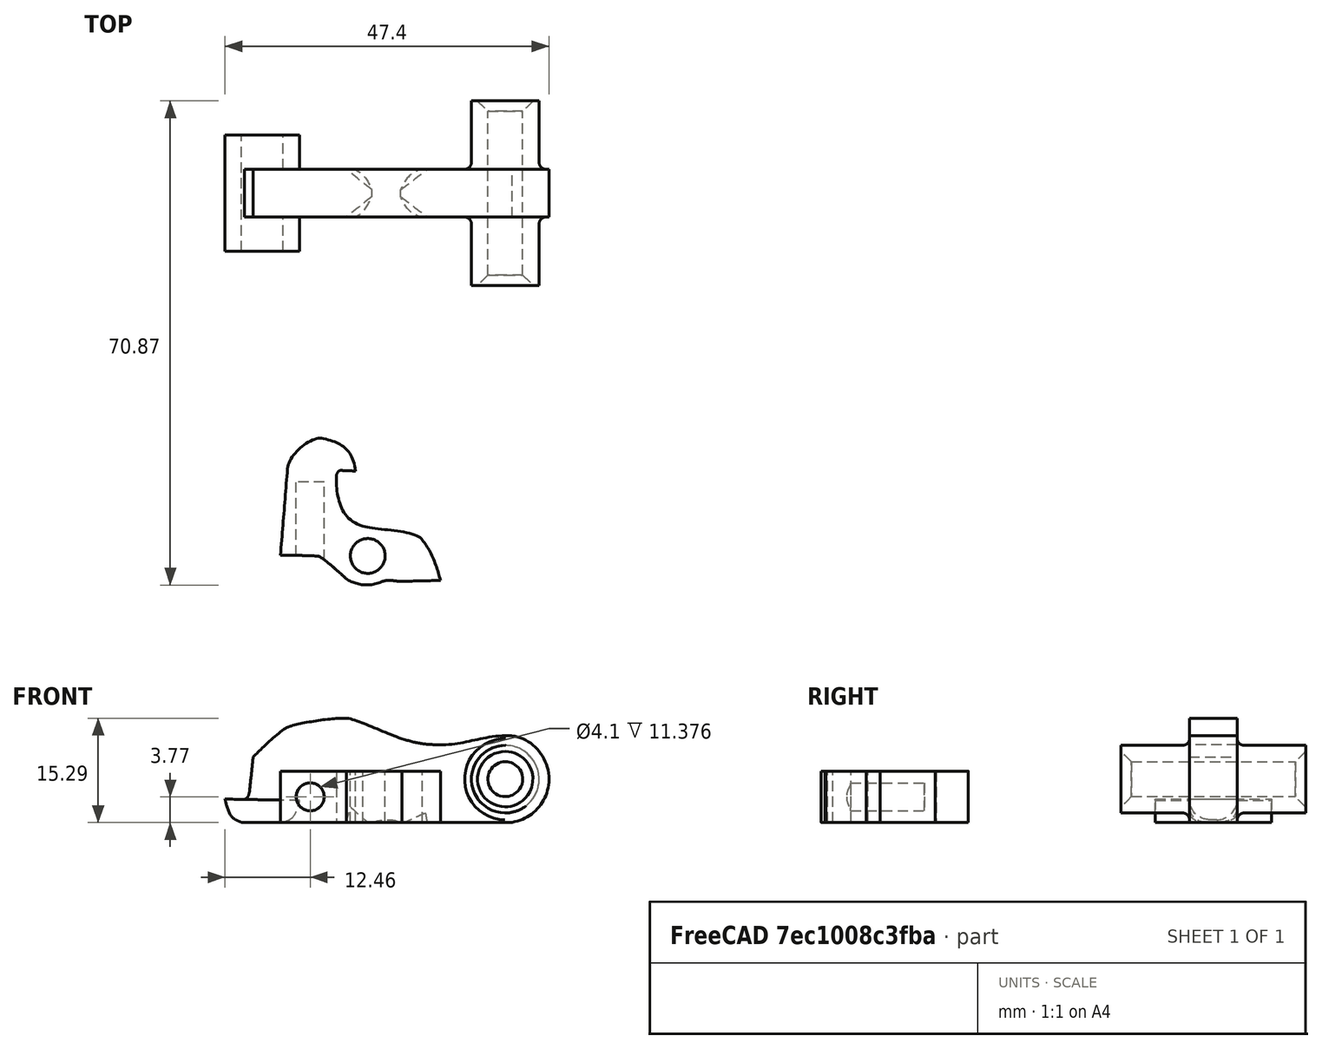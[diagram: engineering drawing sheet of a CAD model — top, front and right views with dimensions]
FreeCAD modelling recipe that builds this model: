
FCSTD DOCUMENT
Label: trace_v7_rev3_simplified
objects: Part::Feature×10, Part::Extrusion×10, Part::Fuse×6, Part::Fillet×3, Part::Cut×3, Part::Cylinder×2, Part::Revolution×1, Part::Chamfer×1, Part::Box×1, Part::MultiCommon×1
note: 38 computed .brp shape members not serialized (recipe doc carries the construction recipe); baked Part::Feature solids carry a one-line shape summary decoded from their .brp

FEATURE [Part::Feature] path3877  label="axispin"
  shape: bbox 35.58 x 3.933 x 2e-07 mm, 0 faces, 0 solids (baked)
FEATURE [Part::Feature] triggerhook
  shape: bbox 39.74 x 27.36 x 2e-07 mm, 1 faces, 0 solids (baked)
FEATURE [Part::Feature] triggerfinger
  shape: bbox 25.29 x 28.76 x 2e-07 mm, 1 faces, 0 solids (baked)
FEATURE [Part::Feature] triggeraxis
  shape: bbox 5.188 x 5.188 x 2e-07 mm, 1 faces, 0 solids (baked)
FEATURE [Part::Feature] discbody
  shape: bbox 26.69 x 23.48 x 2e-07 mm, 1 faces, 0 solids (baked)
FEATURE [Part::Feature] discaxis
  shape: bbox 5.358 x 5.358 x 2e-07 mm, 1 faces, 0 solids (baked)
FEATURE [Part::Feature] hammer_body
  Placement = pos=(0,0,0) rot=(1,0,0;1.5708rad)
  shape: bbox 45.18 x 2e-07 x 15.27 mm, 1 faces, 0 solids (baked)
FEATURE [Part::Feature] hammer_axis_out
  Placement = pos=(0,0,0) rot=(1,0,0;1.5708rad)
  shape: bbox 10.21 x 3.1e-07 x 10.2 mm, 1 faces, 0 solids (baked)
FEATURE [Part::Feature] hammerhooks
  Placement = pos=(0,0,0) rot=(1,0,0;1.5708rad)
  shape: bbox 10.94 x 2e-07 x 3.42 mm, 1 faces, 0 solids (baked)
FEATURE [Part::Feature] hammeraxis
  Placement = pos=(0,0,0) rot=(1,0,0;1.5708rad)
  shape: bbox 5.258 x 2e-07 x 5.257 mm, 1 faces, 0 solids (baked)
FEATURE [Part::Revolution] Revolve  label="axispinR"
  Angle = 360
  Axis = (1,0,0)
  Base = (0,0,0)
  Placement = pos=(10,-3,146.24) rot=(0,1,0;1.5708rad)
  Source = -> path3877
FEATURE [Part::Extrusion] Extrude  label="hammeraxisE"
  Base = -> hammeraxis
  Dir = (0,40,0)
  Placement = pos=(0,-20,0) rot=(0,0,1;0rad)
FEATURE [Part::Extrusion] Extrude001  label="hammeroutE"
  Base = -> hammer_axis_out
  Dir = (0,27,0)
  Placement = pos=(0,-13.5,0) rot=(0,0,1;0rad)
FEATURE [Part::Extrusion] Extrude002  label="hammerbodyE"
  Base = -> hammer_body
  Dir = (0,7,0)
  Placement = pos=(0,-3.5,0) rot=(0,0,1;0rad)
FEATURE [Part::Extrusion] Extrude003  label="hammerhooksE"
  Base = -> hammerhooks
  Dir = (0,17,0)
  Placement = pos=(0,-8.5,0) rot=(0,0,1;0rad)
FEATURE [Part::Fuse] Fusion  label="hammerbits"
  Base = -> Extrude001
  Tool = -> Extrude003
FEATURE [Part::Fuse] Fusion001  label="hammerbodyP"
  Base = -> Extrude002
  Tool = -> Fusion
FEATURE [Part::Fillet] Fillet
  Base = -> Fusion001
  Edges = 2 edges r=3: [Edge16,Edge32]
FEATURE [Part::Fillet] Fillet001
  Base = -> Fillet
  Edges = 4 edges r=1: [Edge20,Edge21,Edge80,Edge81]
FEATURE [Part::Cut] Cut
  Base = -> Fillet001
  Tool = -> Extrude
FEATURE [Part::Chamfer] Chamfer  label="Hammer"
  Base = -> Cut
  Edges = 4 edges r=1.5: [Edge75,Edge76,Edge103,Edge105]
  Placement = pos=(-60,25,6.38) rot=(0,0,1;0rad)
FEATURE [Part::Cylinder] Cylinder  label="discspring"
  Angle = 360
  Height = 11.7
  Placement = pos=(0,-1,-0.7) rot=(-1,0,0;1.5708rad)
  Radius = 2.05
FEATURE [Part::Extrusion] Extrude004  label="discaxisE"
  Base = -> discaxis
  Dir = (0,0,40)
  Placement = pos=(0,0,-20) rot=(0,0,1;0rad)
FEATURE [Part::Fuse] Fusion002  label="discholes"
  Base = -> Cylinder
  Tool = -> Extrude004
FEATURE [Part::Extrusion] Extrude005  label="discbodyE"
  Base = -> discbody
  Dir = (0,0,7.5)
  Placement = pos=(0,0,-4.45) rot=(0,0,1;0rad)
FEATURE [Part::Cut] Cut001  label="Disconnector"
  Base = -> Extrude005
  Placement = pos=(13,-28,4.45) rot=(0,0,1;0rad)
  Tool = -> Fusion002
FEATURE [Part::Extrusion] Extrude006  label="triggerAxisR"
  Base = -> triggeraxis
  Dir = (0,0,40)
  Placement = pos=(0,0,-20) rot=(0,0,1;0rad)
FEATURE [Part::Cylinder] Cylinder001  label="triggerspringHole"
  Angle = 360
  Height = 10
  Placement = pos=(34.9,-6.8,0) rot=(-1,0,0;1.5708rad)
  Radius = 2.05
FEATURE [Part::Fuse] Fusion003  label="TriggerHoles"
  Base = -> Extrude006
  Tool = -> Cylinder001
FEATURE [Part::Extrusion] Extrude007  label="TriggerFinger"
  Base = -> triggerfinger
  Dir = (0,0,14)
  Placement = pos=(0,0,-7.65) rot=(0,0,1;0rad)
FEATURE [Part::Extrusion] Extrude008  label="TriggerHookL"
  Base = -> triggerhook
  Dir = (0,0,2.9)
  Placement = pos=(0,0,-7.65) rot=(0,0,1;0rad)
FEATURE [Part::Extrusion] Extrude009  label="TriggerHookR"
  Base = -> triggerhook
  Dir = (0,0,2.9)
  Placement = pos=(0,0,4.25) rot=(0,0,1;0rad)
FEATURE [Part::Fuse] Fusion004  label="TriggerHooks"
  Base = -> Extrude008
  Tool = -> Extrude009
FEATURE [Part::Fuse] Fusion005  label="TriggerMain"
  Base = -> Extrude007
  Tool = -> Fusion004
FEATURE [Part::Cut] Cut002  label="Trigger"
  Base = -> Fusion005
  Placement = pos=(0,0,7.65) rot=(0,0,1;0rad)
  Tool = -> Fusion003
FEATURE [Part::Box] Box  label="TriggerTipTrim"
  Height = 14.5
  Length = 80
  Placement = pos=(31,-46,0) rot=(0,0,1;0.523599rad)
  Width = 80
FEATURE [Part::Fillet] Fillet002  label="TriggerTipTrimF"
  Base = -> Box
  Edges = 2 edges r=7: [Edge9,Edge10]
FEATURE [Part::MultiCommon] Common  label="TriggerAll"
  Shapes = -> [Fillet002,Cut002]
